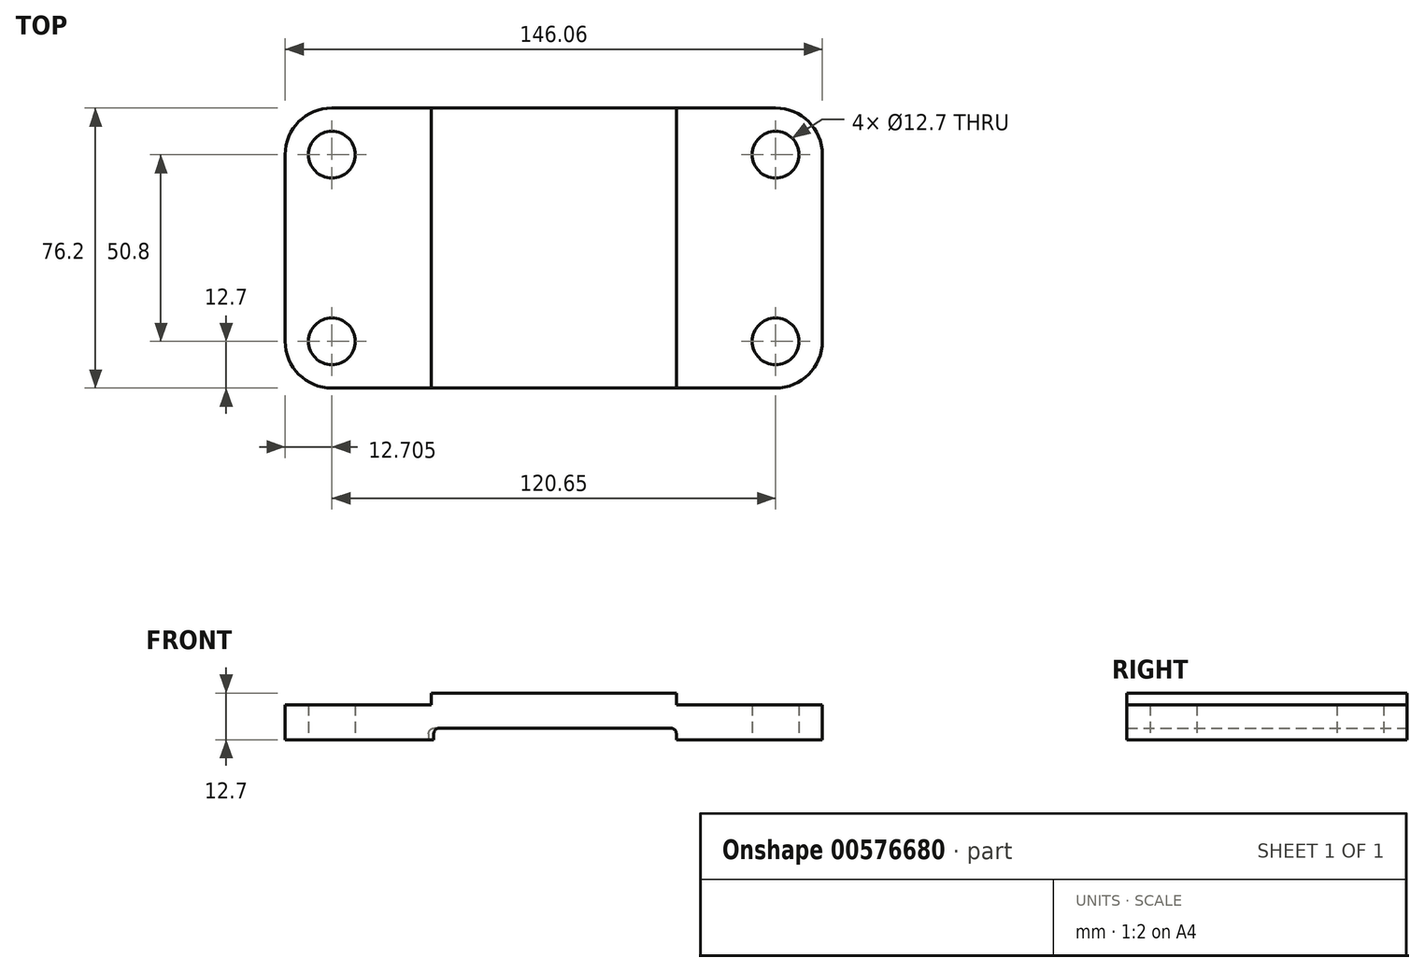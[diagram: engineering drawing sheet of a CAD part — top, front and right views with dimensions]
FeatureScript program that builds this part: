
annotation { "Feature Type Name" : "Feature", "Feature Type Description" : "" }
export const myFeature = defineFeature(function(context is Context, id is Id, definition is map)
    precondition{}
    {
        {
            var Q0;
            Q0=qCreatedBy(makeId("Top.planeOp"),FACE);
            var sketch = newSketch(context, id + "F0", { "sketchPlane" : qUnion([Q0])});
            skLineSegment(sketch, "E0.bottom", {"start": v(-60.32, 38.1) * mm, "end": v(60.33, 38.1) * mm});
            skLineSegment(sketch, "E0.top", {"start": v(-60.33, -38.1) * mm, "end": v(60.33, -38.1) * mm});
            skLineSegment(sketch, "E0.left", {"start": v(-73.02, 25.4) * mm, "end": v(-73.03, -25.4) * mm});
            skLineSegment(sketch, "E0.right", {"start": v(73.03, 25.4) * mm, "end": v(73.03, -25.4) * mm});
            skPoint(sketch, "E0.middle", {"position": v(0, 0) * mm});
            skPoint(sketch, "E1.visualSharp", {"position": v(-73.02, 38.1) * mm});
            skArc(sketch, "E1.filletArc", {"start": v(-60.33, 38.1) * mm, "mid": v(-69.3, 34.38) * mm, "end": v(-73.03, 25.4) * mm});
            skPoint(sketch, "E2.visualSharp", {"position": v(73.03, 38.1) * mm});
            skArc(sketch, "E2.filletArc", {"start": v(73.03, 25.4) * mm, "mid": v(69.3, 34.38) * mm, "end": v(60.33, 38.1) * mm});
            skPoint(sketch, "E3.visualSharp", {"position": v(73.03, -38.1) * mm});
            skArc(sketch, "E3.filletArc", {"start": v(60.33, -38.1) * mm, "mid": v(69.3, -34.38) * mm, "end": v(73.03, -25.4) * mm});
            skPoint(sketch, "E4.visualSharp", {"position": v(-73.03, -38.1) * mm});
            skArc(sketch, "E4.filletArc", {"start": v(-73.03, -25.4) * mm, "mid": v(-69.3, -34.38) * mm, "end": v(-60.33, -38.1) * mm});
            skCircle(sketch, "E5", {"center": v(-60.33, 25.4) * mm, "radius": 6.35 * mm});
            skCircle(sketch, "E6", {"center": v(60.33, 25.4) * mm, "radius": 6.35 * mm});
            skCircle(sketch, "E7", {"center": v(-60.33, -25.4) * mm, "radius": 6.35 * mm});
            skCircle(sketch, "E8", {"center": v(60.33, -25.4) * mm, "radius": 6.35 * mm});
            skLineSegment(sketch, "E9", {"start": v(-33.34, 38.1) * mm, "end": v(-33.34, -38.1) * mm});
            skLineSegment(sketch, "E10", {"start": v(33.34, 38.1) * mm, "end": v(33.34, -38.1) * mm});
            skSolve(sketch);
        }
        {
            var Q0;
            {var subQ0=sQuery(id+"F0.wireOp",EDGE,"E9");Q0=makeQuery(id+"F0.imprint","IMPRINT",FACE,{"disambiguationData":[TD([[makeQuery(id+"F0.imprint","IMPRINT",EDGE,{"derivedFrom":subQ0}),1.0]])]});}
            var Q1;
            Q1=makeQuery(id+"F0.imprint","IMPRINT",FACE,{"disambiguationData":[TD([[makeQuery(id+"F0.imprint","IMPRINT",EDGE,{"derivedFrom":sQuery(id+"F0.wireOp",EDGE,"E0.right")}),-1.0]])]});
            var Q2;
            Q2=makeQuery(id+"F0.imprint","IMPRINT",FACE,{"disambiguationData":[TD([[makeQuery(id+"F0.imprint","IMPRINT",EDGE,{"derivedFrom":sQuery(id+"F0.wireOp",EDGE,"E0.left")}),1.0]])]});
            extrude(context, id + "F1", {"entities" : qUnion([Q0, Q1, Q2]), "depth" : 9.52 * mm, "offsetDistance" : 25.4 * mm});
        }
        {
            var Q0;
            Q0=makeQuery(id+"F1.opExtrude","CAP_FACE",FACE,{"disambiguationData":[OSD([sQuery(id+"F0.wireOp",EDGE,"E0.bottom"),sQuery(id+"F0.wireOp",EDGE,"E0.top"),sQuery(id+"F0.wireOp",EDGE,"E0.left"),sQuery(id+"F0.wireOp",EDGE,"E0.right"),sQuery(id+"F0.wireOp",EDGE,"E1.filletArc"),sQuery(id+"F0.wireOp",EDGE,"E2.filletArc"),sQuery(id+"F0.wireOp",EDGE,"E3.filletArc"),sQuery(id+"F0.wireOp",EDGE,"E4.filletArc"),sQuery(id+"F0.wireOp",EDGE,"E5"),sQuery(id+"F0.wireOp",EDGE,"E6"),sQuery(id+"F0.wireOp",EDGE,"E7"),sQuery(id+"F0.wireOp",EDGE,"E8")])],"isStart":false});
            var sketch = newSketch(context, id + "F2", { "sketchPlane" : qUnion([Q0])});
            skLineSegment(sketch, "E11", {"start": v(-33.34, -38.1) * mm, "end": v(-33.34, 38.1) * mm});
            skLineSegment(sketch, "E12", {"start": v(33.34, -38.1) * mm, "end": v(33.34, 38.1) * mm});
            skSolve(sketch);
        }
        {
            var Q0;
            Q0 = qSketchRegion(id + "F2", true);
            var Q1;
            {var subQ0=sQuery(id+"F2.wireOp",EDGE,"E11");Q1=makeQuery(id+"F2.imprint","IMPRINT",FACE,{"disambiguationData":[TD([[makeQuery(id+"F2.imprint","IMPRINT",EDGE,{"derivedFrom":subQ0}),-1.0]])]});}
            extrude(context, id + "F3", {"entities" : qUnion([Q0, Q1]), "operationType" : NewBodyOperationType.ADD, "depth" : 3.17 * mm, "offsetDistance" : 25.4 * mm});
        }
        {
            var Q0;
            Q0=makeQuery(id+"F1.opExtrude","CAP_FACE",FACE,{"disambiguationData":[OSD([sQuery(id+"F0.wireOp",EDGE,"E0.bottom"),sQuery(id+"F0.wireOp",EDGE,"E0.top"),sQuery(id+"F0.wireOp",EDGE,"E0.left"),sQuery(id+"F0.wireOp",EDGE,"E0.right"),sQuery(id+"F0.wireOp",EDGE,"E1.filletArc"),sQuery(id+"F0.wireOp",EDGE,"E2.filletArc"),sQuery(id+"F0.wireOp",EDGE,"E3.filletArc"),sQuery(id+"F0.wireOp",EDGE,"E4.filletArc"),sQuery(id+"F0.wireOp",EDGE,"E5"),sQuery(id+"F0.wireOp",EDGE,"E6"),sQuery(id+"F0.wireOp",EDGE,"E7"),sQuery(id+"F0.wireOp",EDGE,"E8")])],"isStart":true});
            var sketch = newSketch(context, id + "F4", { "sketchPlane" : qUnion([Q0])});
            skLineSegment(sketch, "E13", {"start": v(33.34, 38.1) * mm, "end": v(33.34, -38.1) * mm});
            skLineSegment(sketch, "E14", {"start": v(-32.63, 38.1) * mm, "end": v(-34.04, -38.1) * mm});
            skSolve(sketch);
        }
        {
            var Q0;
            Q0 = qSketchRegion(id + "F4", true);
            var Q1;
            {var subQ0=sQuery(id+"F4.wireOp",EDGE,"E13");Q1=makeQuery(id+"F4.imprint","IMPRINT",FACE,{"disambiguationData":[TD([[makeQuery(id+"F4.imprint","IMPRINT",EDGE,{"derivedFrom":subQ0}),-1.0]])]});}
            extrude(context, id + "F5", {"entities" : qUnion([Q0, Q1]), "operationType" : NewBodyOperationType.REMOVE, "oppositeDirection" : true, "depth" : 3.17 * mm, "offsetDistance" : 25.4 * mm});
        }
        {
            var Q0;
            Q0=makeQuery(id+"F5.boolean.opBoolean","COPY",EDGE,{"derivedFrom":makeQuery(id+"F5.opExtrude","CAP_EDGE",EDGE,{"disambiguationData":[OSD([sQuery(id+"F4.wireOp",EDGE,"E13")])],"isStart":false})});
            var Q1;
            Q1=makeQuery(id+"F5.boolean.opBoolean","COPY",EDGE,{"derivedFrom":makeQuery(id+"F5.opExtrude","CAP_EDGE",EDGE,{"disambiguationData":[OSD([sQuery(id+"F4.wireOp",EDGE,"E14")])],"isStart":false})});
            fillet(context, id + "F6", {"entities" : qUnion([Q0, Q1]), "radius" : 1.59 * mm, "tangentPropagation" : true, "allowEdgeOverflow" : false});
        }
    });
